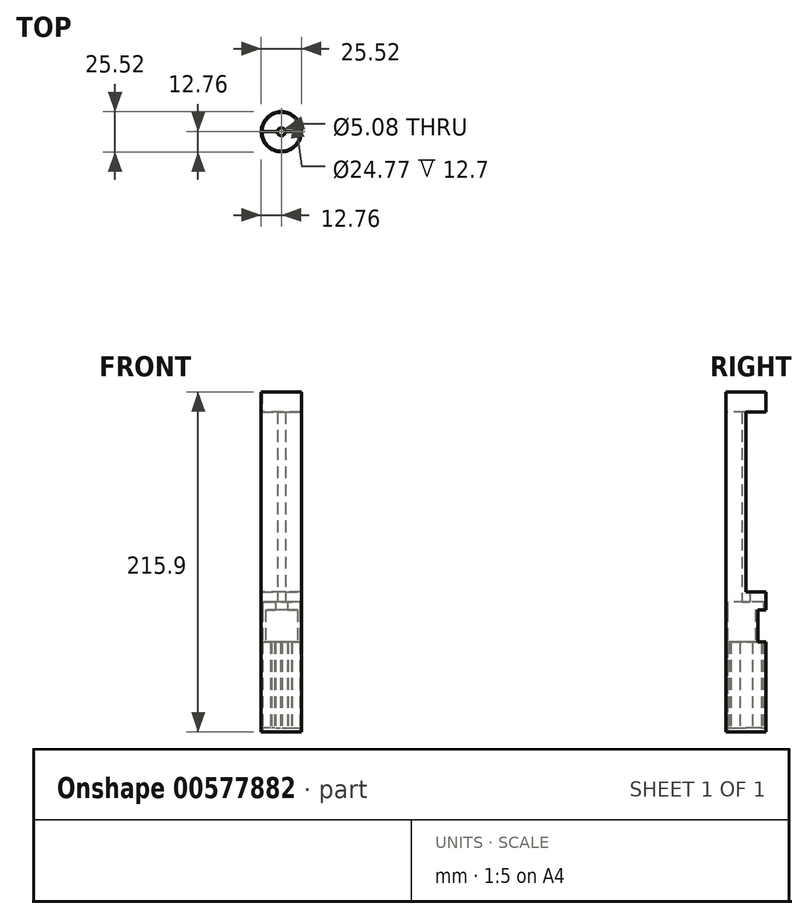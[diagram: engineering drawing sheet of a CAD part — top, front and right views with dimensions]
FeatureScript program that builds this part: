
annotation { "Feature Type Name" : "Feature", "Feature Type Description" : "" }
export const myFeature = defineFeature(function(context is Context, id is Id, definition is map)
    precondition{}
    {
        {
            var Q0;
            Q0=qCreatedBy(makeId("Top.planeOp"),FACE);
            var sketch = newSketch(context, id + "F0", { "sketchPlane" : qUnion([Q0])});
            skArc(sketch, "E0", {"start": v(-3.8, 11.18) * mm, "mid": v(0, -11.81) * mm, "end": v(3.81, 11.18) * mm});
            skCircle(sketch, "E1", {"center": v(0, 0) * mm, "radius": 12.76 * mm});
            skArc(sketch, "E2", {"start": v(3.8, 11.85) * mm, "mid": v(0, 12.45) * mm, "end": v(-3.8, 11.85) * mm});
            skLineSegment(sketch, "E3", {"start": v(3.81, 11.18) * mm, "end": v(3.81, 11.85) * mm});
            skLineSegment(sketch, "E4", {"start": v(-3.81, 11.18) * mm, "end": v(-3.81, 11.85) * mm});
            skSolve(sketch);
        }
        {
            var Q0;
            Q0 = qSketchRegion(id + "F0", true);
            extrude(context, id + "F1", {"entities" : qUnion([Q0]), "depth" : 2.54 * mm, "offsetDistance" : 25.4 * mm});
        }
        {
            var Q0;
            Q0=makeQuery(id+"F1.opExtrude","CAP_FACE",FACE,{"disambiguationData":[OSD([sQuery(id+"F0.wireOp",EDGE,"E0"),sQuery(id+"F0.wireOp",EDGE,"E1"),sQuery(id+"F0.wireOp",EDGE,"E2"),sQuery(id+"F0.wireOp",EDGE,"E3"),sQuery(id+"F0.wireOp",EDGE,"E4")])],"isStart":false});
            var sketch = newSketch(context, id + "F2", { "sketchPlane" : qUnion([Q0])});
            skCircle(sketch, "E5", {"center": v(0, 0) * mm, "radius": 12.76 * mm});
            skArc(sketch, "E6", {"start": v(6.73, -10.47) * mm, "mid": v(9.83, -7.63) * mm, "end": v(11.81, -3.92) * mm});
            skArc(sketch, "E7", {"start": v(-6.73, -9.7) * mm, "mid": v(-6.54, -9.83) * mm, "end": v(-6.35, -9.96) * mm});
            skLineSegment(sketch, "E8", {"start": v(3.81, 11.18) * mm, "end": v(3.81, 11.85) * mm});
            skLineSegment(sketch, "E9", {"start": v(4.2, 11.04) * mm, "end": v(4.2, 11.72) * mm});
            skLineSegment(sketch, "E10", {"start": v(-3.81, 11.18) * mm, "end": v(-3.81, 11.85) * mm});
            skLineSegment(sketch, "E11", {"start": v(-4.2, 11.04) * mm, "end": v(-4.2, 11.72) * mm});
            skLineSegment(sketch, "E12", {"start": v(-6.35, 9.96) * mm, "end": v(-6.35, 10.7) * mm});
            skLineSegment(sketch, "E13", {"start": v(-6.73, 9.7) * mm, "end": v(-6.73, 10.47) * mm});
            skPoint(sketch, "E14.endSnap0", {"position": v(1.9, 0) * mm});
            skLineSegment(sketch, "E15", {"start": v(6.35, 9.96) * mm, "end": v(6.35, 10.7) * mm});
            skLineSegment(sketch, "E16", {"start": v(6.73, 9.7) * mm, "end": v(6.73, 10.47) * mm});
            skLineSegment(sketch, "E17", {"start": v(-3.81, -11.18) * mm, "end": v(-3.81, -11.85) * mm});
            skLineSegment(sketch, "E18", {"start": v(-4.2, -11.04) * mm, "end": v(-4.2, -11.72) * mm});
            skLineSegment(sketch, "E19", {"start": v(-6.35, -9.96) * mm, "end": v(-6.35, -10.7) * mm});
            skLineSegment(sketch, "E20", {"start": v(-6.73, -9.7) * mm, "end": v(-6.73, -10.47) * mm});
            skLineSegment(sketch, "E21", {"start": v(3.81, -11.18) * mm, "end": v(3.81, -11.85) * mm});
            skLineSegment(sketch, "E22", {"start": v(4.2, -11.04) * mm, "end": v(4.2, -11.72) * mm});
            skLineSegment(sketch, "E23", {"start": v(6.35, -9.96) * mm, "end": v(6.35, -10.7) * mm});
            skLineSegment(sketch, "E24", {"start": v(6.73, -9.7) * mm, "end": v(6.73, -10.47) * mm});
            skLineSegment(sketch, "E25", {"start": v(-11.81, 0) * mm, "end": v(-11.81, 3.92) * mm});
            skLineSegment(sketch, "E26", {"start": v(-11.81, 3.92) * mm, "end": v(-11.81, -3.92) * mm});
            skLineSegment(sketch, "E27", {"start": v(11.81, 0) * mm, "end": v(11.81, 3.92) * mm});
            skLineSegment(sketch, "E28", {"start": v(11.81, 3.92) * mm, "end": v(11.81, -3.92) * mm});
            skArc(sketch, "E29.trimOffspring", {"start": v(-4.2, -11.04) * mm, "mid": v(-4, -11.11) * mm, "end": v(-3.81, -11.18) * mm});
            skArc(sketch, "E30.trimOffspring", {"start": v(3.8, -11.18) * mm, "mid": v(4, -11.11) * mm, "end": v(4.2, -11.04) * mm});
            skArc(sketch, "E31.trimOffspring", {"start": v(6.35, -9.96) * mm, "mid": v(6.54, -9.83) * mm, "end": v(6.73, -9.7) * mm});
            skArc(sketch, "E32.trimOffspring", {"start": v(6.73, 9.7) * mm, "mid": v(6.54, 9.83) * mm, "end": v(6.35, 9.96) * mm});
            skArc(sketch, "E33.trimOffspring", {"start": v(4.2, 11.04) * mm, "mid": v(4, 11.11) * mm, "end": v(3.81, 11.18) * mm});
            skArc(sketch, "E34.trimOffspring", {"start": v(-3.8, 11.18) * mm, "mid": v(-4, 11.11) * mm, "end": v(-4.2, 11.04) * mm});
            skArc(sketch, "E35.trimOffspring", {"start": v(-6.35, 9.96) * mm, "mid": v(-6.54, 9.83) * mm, "end": v(-6.73, 9.7) * mm});
            skPoint(sketch, "E36.start.orphan", {"position": v(3.81, 0) * mm});
            skPoint(sketch, "E37.start.orphan", {"position": v(6.35, 0) * mm});
            skPoint(sketch, "E38.start.orphan", {"position": v(-3.81, 0) * mm});
            skArc(sketch, "E39.trimOffspring", {"start": v(4.2, -11.72) * mm, "mid": v(5.3, -11.26) * mm, "end": v(6.35, -10.7) * mm});
            skArc(sketch, "E40.trimOffspring", {"start": v(-3.8, -11.85) * mm, "mid": v(-2.12, -12.26) * mm, "end": v(-0.38, -12.44) * mm});
            skArc(sketch, "E41.trimOffspring", {"start": v(-6.35, -10.7) * mm, "mid": v(-5.3, -11.26) * mm, "end": v(-4.2, -11.72) * mm});
            skArc(sketch, "E42.trimOffspring", {"start": v(11.81, 3.92) * mm, "mid": v(9.83, 7.63) * mm, "end": v(6.73, 10.47) * mm});
            skArc(sketch, "E43.trimOffspring", {"start": v(-11.81, -3.92) * mm, "mid": v(-9.83, -7.63) * mm, "end": v(-6.73, -10.47) * mm});
            skArc(sketch, "E44.trimOffspring", {"start": v(-6.73, 10.47) * mm, "mid": v(-9.83, 7.63) * mm, "end": v(-11.81, 3.92) * mm});
            skArc(sketch, "E45.trimOffspring", {"start": v(-4.2, 11.72) * mm, "mid": v(-5.3, 11.26) * mm, "end": v(-6.35, 10.7) * mm});
            skArc(sketch, "E46.trimOffspring", {"start": v(3.8, 11.85) * mm, "mid": v(0, 12.45) * mm, "end": v(-3.8, 11.85) * mm});
            skArc(sketch, "E47.trimOffspring", {"start": v(6.35, 10.7) * mm, "mid": v(5.3, 11.26) * mm, "end": v(4.2, 11.72) * mm});
            skLineSegment(sketch, "E48", {"start": v(0, 0) * mm, "end": v(0.38, 0) * mm});
            skLineSegment(sketch, "E49", {"start": v(0, 0) * mm, "end": v(-0.38, 0) * mm});
            skLineSegment(sketch, "E50", {"start": v(-0.38, -11.8) * mm, "end": v(-0.38, -12.44) * mm});
            skLineSegment(sketch, "E51", {"start": v(0.38, -11.8) * mm, "end": v(0.38, -12.44) * mm});
            skArc(sketch, "E52", {"start": v(-0.38, -11.8) * mm, "mid": v(0, -11.81) * mm, "end": v(0.38, -11.8) * mm});
            skArc(sketch, "E53.trimOffspring", {"start": v(0.38, -12.44) * mm, "mid": v(2.12, -12.26) * mm, "end": v(3.8, -11.85) * mm});
            skArc(sketch, "E54.trimOffspring", {"start": v(3.81, -11.18) * mm, "mid": v(4, -11.11) * mm, "end": v(4.2, -11.04) * mm});
            skSolve(sketch);
        }
        {
            var Q0;
            Q0 = qSketchRegion(id + "F2", true);
            extrude(context, id + "F3", {"entities" : qUnion([Q0]), "operationType" : NewBodyOperationType.ADD, "depth" : 54.6 * mm, "offsetDistance" : 25.4 * mm});
        }
        {
            var Q0;
            Q0=makeQuery(id+"F3.opExtrude","CAP_FACE",FACE,{"disambiguationData":[OSD([sQuery(id+"F2.wireOp",EDGE,"E5"),sQuery(id+"F2.wireOp",EDGE,"E6"),sQuery(id+"F2.wireOp",EDGE,"E8"),sQuery(id+"F2.wireOp",EDGE,"E9"),sQuery(id+"F2.wireOp",EDGE,"E10"),sQuery(id+"F2.wireOp",EDGE,"E11"),sQuery(id+"F2.wireOp",EDGE,"E12"),sQuery(id+"F2.wireOp",EDGE,"E13"),sQuery(id+"F2.wireOp",EDGE,"E15"),sQuery(id+"F2.wireOp",EDGE,"E16"),sQuery(id+"F2.wireOp",EDGE,"E17"),sQuery(id+"F2.wireOp",EDGE,"E18"),sQuery(id+"F2.wireOp",EDGE,"E19"),sQuery(id+"F2.wireOp",EDGE,"E20"),sQuery(id+"F2.wireOp",EDGE,"E21"),sQuery(id+"F2.wireOp",EDGE,"E22"),sQuery(id+"F2.wireOp",EDGE,"E23"),sQuery(id+"F2.wireOp",EDGE,"E24"),sQuery(id+"F2.wireOp",EDGE,"E26"),sQuery(id+"F2.wireOp",EDGE,"E28"),sQuery(id+"F2.wireOp",EDGE,"E39.trimOffspring"),sQuery(id+"F2.wireOp",EDGE,"E40.trimOffspring"),sQuery(id+"F2.wireOp",EDGE,"E41.trimOffspring"),sQuery(id+"F2.wireOp",EDGE,"E42.trimOffspring"),sQuery(id+"F2.wireOp",EDGE,"E43.trimOffspring"),sQuery(id+"F2.wireOp",EDGE,"E44.trimOffspring"),sQuery(id+"F2.wireOp",EDGE,"E45.trimOffspring"),sQuery(id+"F2.wireOp",EDGE,"E46.trimOffspring"),sQuery(id+"F2.wireOp",EDGE,"E47.trimOffspring"),sQuery(id+"F2.wireOp",EDGE,"E50"),sQuery(id+"F2.wireOp",EDGE,"E51"),sQuery(id+"F2.wireOp",EDGE,"E52"),sQuery(id+"F2.wireOp",EDGE,"E53.trimOffspring"),sQuery(id+"F2.wireOp",EDGE,"E29.trimOffspring"),sQuery(id+"F2.wireOp",EDGE,"E7"),sQuery(id+"F2.wireOp",EDGE,"E54.trimOffspring"),sQuery(id+"F2.wireOp",EDGE,"E31.trimOffspring"),sQuery(id+"F2.wireOp",EDGE,"E32.trimOffspring"),sQuery(id+"F2.wireOp",EDGE,"E33.trimOffspring"),sQuery(id+"F2.wireOp",EDGE,"E34.trimOffspring"),sQuery(id+"F2.wireOp",EDGE,"E35.trimOffspring")])],"isStart":false});
            var sketch = newSketch(context, id + "F4", { "sketchPlane" : qUnion([Q0])});
            skArc(sketch, "E55", {"start": v(-10.16, 7.73) * mm, "mid": v(0, -12.76) * mm, "end": v(10.16, 7.73) * mm});
            skPoint(sketch, "E56.endSnap0", {"position": v(-11.81, 0) * mm});
            skLineSegment(sketch, "E57", {"start": v(-10.16, 6.02) * mm, "end": v(-10.16, 7.73) * mm});
            skLineSegment(sketch, "E58", {"start": v(10.16, 6.02) * mm, "end": v(10.16, 7.73) * mm});
            skArc(sketch, "E59", {"start": v(-10.16, 6.02) * mm, "mid": v(0, -11.81) * mm, "end": v(10.16, 6.02) * mm});
            skPoint(sketch, "E56.end.orphan", {"position": v(-10.16, 0) * mm});
            skSolve(sketch);
        }
        {
            var Q0;
            Q0 = qSketchRegion(id + "F4", true);
            extrude(context, id + "F5", {"entities" : qUnion([Q0]), "operationType" : NewBodyOperationType.ADD, "depth" : 20.32 * mm, "offsetDistance" : 25.4 * mm});
        }
        {
            var Q0;
            Q0=makeQuery(id+"F5.opExtrude","CAP_FACE",FACE,{"disambiguationData":[OSD([sQuery(id+"F4.wireOp",EDGE,"E55"),sQuery(id+"F4.wireOp",EDGE,"E57"),sQuery(id+"F4.wireOp",EDGE,"E58"),sQuery(id+"F4.wireOp",EDGE,"E59")])],"isStart":false});
            var sketch = newSketch(context, id + "F6", { "sketchPlane" : qUnion([Q0])});
            skCircle(sketch, "E60", {"center": v(0, 0) * mm, "radius": 12.76 * mm});
            skArc(sketch, "E61", {"start": v(-3.8, 11.17) * mm, "mid": v(0, -11.8) * mm, "end": v(3.81, 11.17) * mm});
            skArc(sketch, "E62", {"start": v(3.8, 11.84) * mm, "mid": v(0, 12.44) * mm, "end": v(-3.81, 11.84) * mm});
            skLineSegment(sketch, "E63", {"start": v(-3.81, 11.17) * mm, "end": v(-3.81, 11.84) * mm});
            skLineSegment(sketch, "E64", {"start": v(3.81, 11.17) * mm, "end": v(3.81, 11.84) * mm});
            skSolve(sketch);
        }
        {
            var Q0;
            Q0 = qSketchRegion(id + "F6", true);
            extrude(context, id + "F7", {"entities" : qUnion([Q0]), "operationType" : NewBodyOperationType.ADD, "depth" : 5.08 * mm, "offsetDistance" : 25.4 * mm});
        }
        {
            var Q0;
            Q0=makeQuery(id+"F7.opExtrude","CAP_FACE",FACE,{"disambiguationData":[OSD([sQuery(id+"F6.wireOp",EDGE,"E60"),sQuery(id+"F6.wireOp",EDGE,"E61"),sQuery(id+"F6.wireOp",EDGE,"E62"),sQuery(id+"F6.wireOp",EDGE,"E63"),sQuery(id+"F6.wireOp",EDGE,"E64")])],"isStart":false});
            var sketch = newSketch(context, id + "F8", { "sketchPlane" : qUnion([Q0])});
            skCircle(sketch, "E65", {"center": v(0, 0) * mm, "radius": 12.76 * mm});
            skCircle(sketch, "E66", {"center": v(0, 0) * mm, "radius": 2.54 * mm});
            skSolve(sketch);
        }
        {
            var Q0;
            Q0 = qSketchRegion(id + "F8", true);
            extrude(context, id + "F9", {"entities" : qUnion([Q0]), "operationType" : NewBodyOperationType.ADD, "depth" : 6.35 * mm, "offsetDistance" : 25.4 * mm});
        }
        {
            var Q0;
            Q0=makeQuery(id+"F9.opExtrude","CAP_FACE",FACE,{"disambiguationData":[OSD([sQuery(id+"F8.wireOp",EDGE,"E65"),sQuery(id+"F8.wireOp",EDGE,"E66")])],"isStart":false});
            var sketch = newSketch(context, id + "F10", { "sketchPlane" : qUnion([Q0])});
            skArc(sketch, "E67", {"start": v(-12.76, 0) * mm, "mid": v(0, -12.76) * mm, "end": v(12.76, 0) * mm});
            skArc(sketch, "E68", {"start": v(-2.54, 0) * mm, "mid": v(0, -2.54) * mm, "end": v(2.54, 0) * mm});
            skLineSegment(sketch, "E69", {"start": v(-12.76, 0) * mm, "end": v(-2.54, 0) * mm});
            skLineSegment(sketch, "E70.trimOffspring", {"start": v(2.54, 0) * mm, "end": v(12.76, 0) * mm});
            skSolve(sketch);
        }
        {
            var Q0;
            Q0 = qSketchRegion(id + "F10", true);
            extrude(context, id + "F11", {"entities" : qUnion([Q0]), "operationType" : NewBodyOperationType.ADD, "depth" : 114.3 * mm, "offsetDistance" : 25.4 * mm});
        }
        {
            var Q0;
            Q0=makeQuery(id+"F11.opExtrude","CAP_FACE",FACE,{"disambiguationData":[OSD([sQuery(id+"F10.wireOp",EDGE,"E67"),sQuery(id+"F10.wireOp",EDGE,"E68"),sQuery(id+"F10.wireOp",EDGE,"E69"),sQuery(id+"F10.wireOp",EDGE,"E70.trimOffspring")])],"isStart":false});
            var sketch = newSketch(context, id + "F12", { "sketchPlane" : qUnion([Q0])});
            skCircle(sketch, "E71", {"center": v(0, 0) * mm, "radius": 12.76 * mm});
            skCircle(sketch, "E72", {"center": v(0, 0) * mm, "radius": 12.38 * mm});
            skSolve(sketch);
        }
        {
            var Q0;
            Q0 = qSketchRegion(id + "F12", true);
            extrude(context, id + "F13", {"entities" : qUnion([Q0]), "operationType" : NewBodyOperationType.ADD, "depth" : 12.7 * mm, "offsetDistance" : 25.4 * mm});
        }
    });
